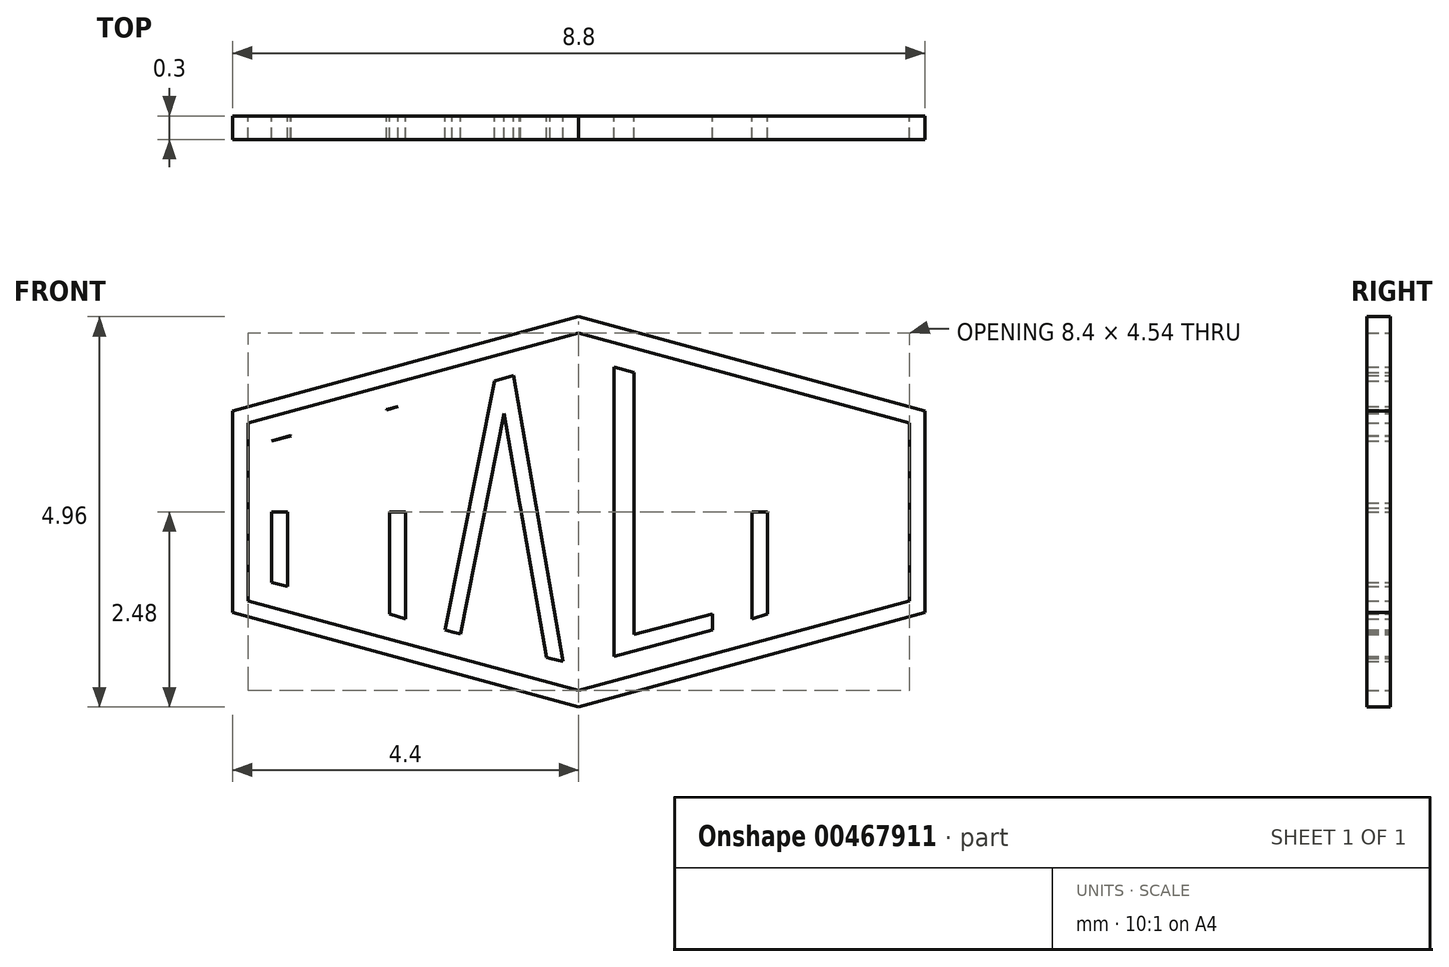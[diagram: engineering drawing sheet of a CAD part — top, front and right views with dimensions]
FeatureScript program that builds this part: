
annotation { "Feature Type Name" : "Feature", "Feature Type Description" : "" }
export const myFeature = defineFeature(function(context is Context, id is Id, definition is map)
    precondition{}
    {
        {
            var Q0;
            Q0=qCreatedBy(makeId("Front.planeOp"),FACE);
            var sketch = newSketch(context, id + "F0", { "sketchPlane" : qUnion([Q0])});
            skLineSegment(sketch, "E0", {"start": v(0, 1.96) * mm, "end": v(-3.9, 0.9) * mm});
            skLineSegment(sketch, "E1", {"start": v(-3.9, 0.9) * mm, "end": v(-3.9, 0) * mm});
            skLineSegment(sketch, "E2.MirrorCS", {"start": v(0, 1.96) * mm, "end": v(3.9, 0.9) * mm});
            skLineSegment(sketch, "E3.MirrorCS", {"start": v(3.9, 0.9) * mm, "end": v(3.9, 0) * mm});
            skLineSegment(sketch, "E4.MirrorCS", {"start": v(0, -1.96) * mm, "end": v(-3.9, -0.9) * mm});
            skLineSegment(sketch, "E5.MirrorCS", {"start": v(3.9, -0.9) * mm, "end": v(3.9, 0) * mm});
            skLineSegment(sketch, "E6.MirrorCS", {"start": v(0, -1.96) * mm, "end": v(3.9, -0.9) * mm});
            skLineSegment(sketch, "E7.MirrorCS", {"start": v(-3.9, -0.9) * mm, "end": v(-3.9, 0) * mm});
            skLineSegment(sketch, "E8", {"start": v(-1.95, 1.43) * mm, "end": v(-1.95, -1.43) * mm});
            skLineSegment(sketch, "E9", {"start": v(1.95, 1.43) * mm, "end": v(1.95, -1.43) * mm});
            skLineSegment(sketch, "E10", {"start": v(-2.2, 1.36) * mm, "end": v(-2.2, -1.36) * mm});
            skLineSegment(sketch, "E11", {"start": v(2.2, 1.36) * mm, "end": v(2.2, -1.36) * mm});
            skLineSegment(sketch, "E12", {"start": v(-1.7, 1.5) * mm, "end": v(-1.7, -1.5) * mm});
            skLineSegment(sketch, "E13", {"start": v(1.7, 1.5) * mm, "end": v(1.7, -1.5) * mm});
            skLineSegment(sketch, "E14", {"start": v(-3.9, -0.9) * mm, "end": v(-3.9, 0.9) * mm});
            skLineSegment(sketch, "E15", {"start": v(-3.9, 0) * mm, "end": v(-2.2, 0) * mm});
            skLineSegment(sketch, "E16", {"start": v(3.9, 0) * mm, "end": v(2.2, 0) * mm});
            skLineSegment(sketch, "E17", {"start": v(-0.2, 1.9) * mm, "end": v(-0.2, -1.9) * mm});
            skLineSegment(sketch, "E18", {"start": v(0.2, 1.9) * mm, "end": v(0.2, -1.9) * mm});
            skLineSegment(sketch, "E19", {"start": v(-0.2, 1.9) * mm, "end": v(-1.7, 1.5) * mm});
            skLineSegment(sketch, "E20", {"start": v(0.2, 1.9) * mm, "end": v(1.7, 1.5) * mm});
            skLineSegment(sketch, "E21", {"start": v(-3.9, 0.9) * mm, "end": v(-3.66, 0.97) * mm});
            skLineSegment(sketch, "E22", {"start": v(-2.2, 1.36) * mm, "end": v(-2.44, 1.3) * mm});
            skPoint(sketch, "E23", {"position": v(-0.95, 1.7) * mm});
            skLineSegment(sketch, "E24", {"start": v(-1.07, 1.66) * mm, "end": v(-0.83, 1.73) * mm});
            skLineSegment(sketch, "E25", {"start": v(-3.05, 0) * mm, "end": v(-3.05, 0.2) * mm});
            skLineSegment(sketch, "E26", {"start": v(-3.05, 0.2) * mm, "end": v(-3.66, 0.97) * mm});
            skLineSegment(sketch, "E27", {"start": v(-3.05, 0.2) * mm, "end": v(-2.44, 1.3) * mm});
            skLineSegment(sketch, "E28", {"start": v(-3.9, -0.9) * mm, "end": v(-3.7, -0.95) * mm});
            skLineSegment(sketch, "E29", {"start": v(-3.7, -0.95) * mm, "end": v(-3.7, 0.7) * mm});
            skLineSegment(sketch, "E30", {"start": v(-3.15, 0) * mm, "end": v(-2.95, 0) * mm});
            skLineSegment(sketch, "E31", {"start": v(-3.7, 0.7) * mm, "end": v(-3.15, 0) * mm});
            skLineSegment(sketch, "E32", {"start": v(-2.2, -1.36) * mm, "end": v(-2.4, -1.3) * mm});
            skLineSegment(sketch, "E33", {"start": v(-2.4, -1.3) * mm, "end": v(-2.4, 1) * mm});
            skLineSegment(sketch, "E34", {"start": v(-2.4, 1) * mm, "end": v(-2.95, 0) * mm});
            skLineSegment(sketch, "E35", {"start": v(-1.7, -1.5) * mm, "end": v(-1.07, 1.66) * mm});
            skLineSegment(sketch, "E36", {"start": v(-0.83, 1.73) * mm, "end": v(-0.2, -1.9) * mm});
            skLineSegment(sketch, "E37", {"start": v(-1.7, -1.5) * mm, "end": v(-1.5, -1.55) * mm});
            skLineSegment(sketch, "E38", {"start": v(-1.5, -1.55) * mm, "end": v(-0.95, 1.25) * mm});
            skLineSegment(sketch, "E39", {"start": v(-0.95, 1.25) * mm, "end": v(-0.41, -1.85) * mm});
            skLineSegment(sketch, "E40", {"start": v(-0.41, -1.85) * mm, "end": v(-0.2, -1.9) * mm});
            skLineSegment(sketch, "E41", {"start": v(-1.18, 0.11) * mm, "end": v(-1.22, -0.09) * mm});
            skLineSegment(sketch, "E42", {"start": v(-1.22, -0.09) * mm, "end": v(-0.72, -0.09) * mm});
            skLineSegment(sketch, "E43", {"start": v(-0.72, -0.09) * mm, "end": v(-0.75, 0.11) * mm});
            skLineSegment(sketch, "E44", {"start": v(-0.75, 0.11) * mm, "end": v(-1.18, 0.11) * mm});
            skLineSegment(sketch, "E45", {"start": v(0.2, 1.9) * mm, "end": v(0.45, 1.84) * mm});
            skLineSegment(sketch, "E46", {"start": v(0.45, 1.84) * mm, "end": v(0.45, -1.63) * mm});
            skLineSegment(sketch, "E47", {"start": v(0.45, -1.63) * mm, "end": v(1.7, -1.3) * mm});
            skLineSegment(sketch, "E48", {"start": v(1.7, -1.3) * mm, "end": v(1.7, -1.5) * mm});
            skLineSegment(sketch, "E49", {"start": v(0.2, -1.9) * mm, "end": v(0.2, 1.9) * mm});
            skSolve(sketch);
        }
        {
            var Q0;
            {var subQ0=sQuery(id+"F0.wireOp",EDGE,"E28");Q0=makeQuery(id+"F0.imprint","IMPRINT",FACE,{"disambiguationData":[TD([[makeQuery(id+"F0.imprint","IMPRINT",EDGE,{"derivedFrom":subQ0}),1.0]])]});}
            var Q1;
            {var subQ6=sQuery(id+"F0.wireOp",EDGE,"E21");Q1=makeQuery(id+"F0.imprint","IMPRINT",FACE,{"disambiguationData":[TD([[makeQuery(id+"F0.imprint","IMPRINT",EDGE,{"derivedFrom":subQ6}),-1.0]])]});}
            var Q2;
            {var subQ0=sQuery(id+"F0.wireOp",EDGE,"E22");Q2=makeQuery(id+"F0.imprint","IMPRINT",FACE,{"disambiguationData":[TD([[makeQuery(id+"F0.imprint","IMPRINT",EDGE,{"derivedFrom":subQ0}),1.0]])]});}
            var Q3;
            {var subQ0=sQuery(id+"F0.wireOp",EDGE,"E32");Q3=makeQuery(id+"F0.imprint","IMPRINT",FACE,{"disambiguationData":[TD([[makeQuery(id+"F0.imprint","IMPRINT",EDGE,{"derivedFrom":subQ0}),-1.0]])]});}
            var Q4;
            Q4=makeQuery(id+"F0.imprint","IMPRINT",FACE,{"disambiguationData":[TD([[makeQuery(id+"F0.imprint","IMPRINT",EDGE,{"derivedFrom":sQuery(id+"F0.wireOp",EDGE,"E24")}),-1.0]])]});
            var Q5;
            Q5=makeQuery(id+"F0.imprint","IMPRINT",FACE,{"disambiguationData":[TD([[makeQuery(id+"F0.imprint","IMPRINT",EDGE,{"derivedFrom":sQuery(id+"F0.wireOp",EDGE,"E41")}),1.0]])]});
            extrude(context, id + "F1", {"entities" : qUnion([Q0, Q1, Q2, Q3, Q4, Q5]), "depth" : 0.3 * mm});
        }
        {
            var Q0;
            Q0=makeQuery(id+"F1.opExtrude","SWEPT_BODY",BODY,{"disambiguationData":[OSD([sQuery(id+"F0.wireOp",EDGE,"E10"),sQuery(id+"F0.wireOp",EDGE,"E14"),sQuery(id+"F0.wireOp",EDGE,"E21"),sQuery(id+"F0.wireOp",EDGE,"E22"),sQuery(id+"F0.wireOp",EDGE,"E26"),sQuery(id+"F0.wireOp",EDGE,"E27"),sQuery(id+"F0.wireOp",EDGE,"E28"),sQuery(id+"F0.wireOp",EDGE,"E29"),sQuery(id+"F0.wireOp",EDGE,"E30"),sQuery(id+"F0.wireOp",EDGE,"E31"),sQuery(id+"F0.wireOp",EDGE,"E32"),sQuery(id+"F0.wireOp",EDGE,"E33"),sQuery(id+"F0.wireOp",EDGE,"E34")])]});
            var Q1;
            Q1=qCreatedBy(makeId("Right.planeOp"),FACE);
            mirror(context, id + "F2", {"entities" : qUnion([Q0]), "mirrorPlane" : qUnion([Q1])});
        }
        {
            var Q0;
            Q0=qCreatedBy(makeId("Front.planeOp"),FACE);
            var sketch = newSketch(context, id + "F3", { "sketchPlane" : qUnion([Q0])});
            skLineSegment(sketch, "E50.0.0", {"start": v(1.7, 1.5) * mm, "end": v(0.45, 1.84) * mm});
            skLineSegment(sketch, "E50.0.1", {"start": v(0.45, 1.84) * mm, "end": v(0.45, -1.63) * mm});
            skLineSegment(sketch, "E50.0.2", {"start": v(0.45, -1.63) * mm, "end": v(1.7, -1.3) * mm});
            skLineSegment(sketch, "E50.0.3", {"start": v(1.7, -1.3) * mm, "end": v(1.7, 1.5) * mm});
            skLineSegment(sketch, "E51.0", {"start": v(0, -1.96) * mm, "end": v(3.9, -0.9) * mm});
            skLineSegment(sketch, "E52.0.0", {"start": v(1.7, 1.5) * mm, "end": v(1.7, -1.3) * mm});
            skLineSegment(sketch, "E52.0.1", {"start": v(1.7, -1.3) * mm, "end": v(1.7, -1.5) * mm});
            skLineSegment(sketch, "E52.0.2", {"start": v(1.7, -1.5) * mm, "end": v(1.95, -1.43) * mm});
            skLineSegment(sketch, "E52.0.3", {"start": v(1.95, -1.43) * mm, "end": v(1.95, 1.43) * mm});
            skLineSegment(sketch, "E52.0.4", {"start": v(1.95, 1.43) * mm, "end": v(1.7, 1.5) * mm});
            skLineSegment(sketch, "E53", {"start": v(0.45, 1.84) * mm, "end": v(0.45, -1.84) * mm});
            skLineSegment(sketch, "E54", {"start": v(0.45, -1.84) * mm, "end": v(1.7, -1.5) * mm});
            skLineSegment(sketch, "E55", {"start": v(1.7, -1.3) * mm, "end": v(0.7, -1.56) * mm});
            skLineSegment(sketch, "E56", {"start": v(0.7, -1.56) * mm, "end": v(0.7, 1.77) * mm});
            skLineSegment(sketch, "E57", {"start": v(0.7, 1.77) * mm, "end": v(0.45, 1.84) * mm});
            skSolve(sketch);
        }
        {
            var Q0;
            {var subQ0=sQuery(id+"F3.wireOp",EDGE,"E50.0.2");Q0=makeQuery(id+"F3.imprint","IMPRINT",FACE,{"disambiguationData":[TD([[makeQuery(id+"F3.imprint","IMPRINT",EDGE,{"derivedFrom":subQ0}),1.0]])]});}
            var Q1;
            {var subQ2=sQuery(id+"F3.wireOp",EDGE,"E50.0.2");Q1=makeQuery(id+"F3.imprint","IMPRINT",FACE,{"disambiguationData":[TD([[makeQuery(id+"F3.imprint","IMPRINT",EDGE,{"derivedFrom":subQ2}),-1.0]])]});}
            extrude(context, id + "F4", {"entities" : qUnion([Q0, Q1]), "depth" : 0.3 * mm});
        }
        {
            var Q0;
            Q0=qCreatedBy(makeId("Front.planeOp"),FACE);
            var sketch = newSketch(context, id + "F5", { "sketchPlane" : qUnion([Q0])});
            skLineSegment(sketch, "E58.0", {"start": v(0, -2.27) * mm, "end": v(-4.2, -1.13) * mm});
            skLineSegment(sketch, "E58.1", {"start": v(-4.2, -1.13) * mm, "end": v(-4.2, 1.13) * mm});
            skLineSegment(sketch, "E58.2", {"start": v(4.2, -1.13) * mm, "end": v(4.2, 0) * mm});
            skLineSegment(sketch, "E58.3", {"start": v(4.2, 1.13) * mm, "end": v(4.2, 0) * mm});
            skLineSegment(sketch, "E58.4", {"start": v(0, 2.27) * mm, "end": v(4.2, 1.13) * mm});
            skLineSegment(sketch, "E58.5", {"start": v(0, -2.27) * mm, "end": v(4.2, -1.13) * mm});
            skLineSegment(sketch, "E58.6", {"start": v(0, 2.27) * mm, "end": v(-4.2, 1.13) * mm});
            skLineSegment(sketch, "E59.0", {"start": v(0, 2.48) * mm, "end": v(4.4, 1.28) * mm});
            skLineSegment(sketch, "E59.1", {"start": v(4.4, 1.28) * mm, "end": v(4.4, 0) * mm});
            skLineSegment(sketch, "E59.2", {"start": v(-4.4, -1.28) * mm, "end": v(-4.4, 1.28) * mm});
            skLineSegment(sketch, "E59.3", {"start": v(0, -2.48) * mm, "end": v(-4.4, -1.28) * mm});
            skLineSegment(sketch, "E59.4", {"start": v(0, -2.48) * mm, "end": v(4.4, -1.28) * mm});
            skLineSegment(sketch, "E59.5", {"start": v(0, 2.48) * mm, "end": v(-4.4, 1.28) * mm});
            skLineSegment(sketch, "E59.6", {"start": v(4.4, -1.28) * mm, "end": v(4.4, 0) * mm});
            skSolve(sketch);
        }
        {
            var Q0;
            Q0=makeQuery(id+"F5.imprint","IMPRINT",FACE,{"disambiguationData":[TD([[makeQuery(id+"F5.imprint","IMPRINT",EDGE,{"derivedFrom":sQuery(id+"F5.wireOp",EDGE,"E58.0")}),1.0]])]});
            extrude(context, id + "F6", {"entities" : qUnion([Q0]), "depth" : 0.3 * mm});
        }
    });
